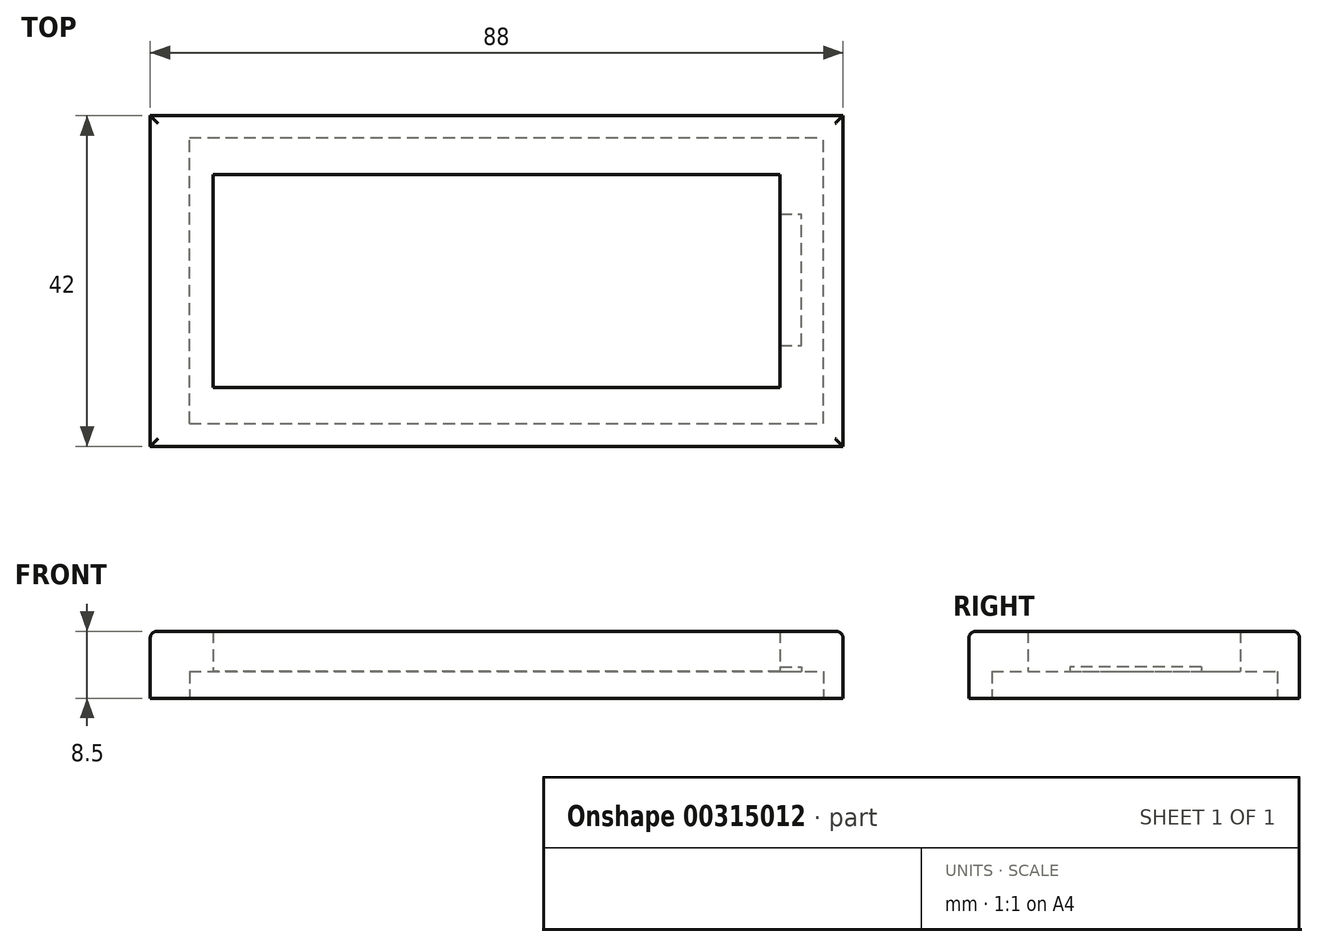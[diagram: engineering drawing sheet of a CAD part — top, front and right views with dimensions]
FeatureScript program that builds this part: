
annotation { "Feature Type Name" : "Feature", "Feature Type Description" : "" }
export const myFeature = defineFeature(function(context is Context, id is Id, definition is map)
    precondition{}
    {
        {
            var Q0;
            Q0=qCreatedBy(makeId("Top.planeOp"),FACE);
            var sketch = newSketch(context, id + "F0", { "sketchPlane" : qUnion([Q0])});
            skLineSegment(sketch, "E0", {"start": v(-44, 21) * mm, "end": v(44, 21) * mm});
            skLineSegment(sketch, "E1", {"start": v(44, 21) * mm, "end": v(44, -21) * mm});
            skLineSegment(sketch, "E2", {"start": v(44, -21) * mm, "end": v(-44, -21) * mm});
            skLineSegment(sketch, "E3", {"start": v(-44, -21) * mm, "end": v(-44, 21) * mm});
            skLineSegment(sketch, "E4.bottom", {"start": v(-36, 13.5) * mm, "end": v(36, 13.5) * mm});
            skLineSegment(sketch, "E4.top", {"start": v(-36, -13.5) * mm, "end": v(36, -13.5) * mm});
            skLineSegment(sketch, "E4.left", {"start": v(-36, 13.5) * mm, "end": v(-36, -13.5) * mm});
            skLineSegment(sketch, "E4.right", {"start": v(36, 13.5) * mm, "end": v(36, -13.5) * mm});
            skLineSegment(sketch, "E5", {"start": v(0, 21) * mm, "end": v(0, 13.5) * mm, "construction": true});
            skPoint(sketch, "E5.endSnap0", {"position": v(0, 13.5) * mm});
            skLineSegment(sketch, "E6", {"start": v(0, -13.5) * mm, "end": v(0, -21) * mm, "construction": true});
            skLineSegment(sketch, "E7", {"start": v(-44, 0) * mm, "end": v(-36, 0) * mm, "construction": true});
            skLineSegment(sketch, "E8", {"start": v(36, 0) * mm, "end": v(44, 0) * mm, "construction": true});
            skLineSegment(sketch, "E9", {"start": v(0, 0) * mm, "end": v(44, 0) * mm, "construction": true});
            skLineSegment(sketch, "E10", {"start": v(0, 0) * mm, "end": v(-44, 0) * mm, "construction": true});
            skLineSegment(sketch, "E11", {"start": v(0, 21) * mm, "end": v(0, -21) * mm, "construction": true});
            skSolve(sketch);
        }
        {
            var Q0;
            Q0=makeQuery(id+"F0.imprint","IMPRINT",FACE,{"disambiguationData":[TD([[makeQuery(id+"F0.imprint","IMPRINT",EDGE,{"derivedFrom":sQuery(id+"F0.wireOp",EDGE,"E0")}),-1.0]])]});
            extrude(context, id + "F1", {"entities" : qUnion([Q0]), "depth" : 8.5 * mm});
        }
        {
            var Q0;
            Q0=makeQuery(id+"F1.opExtrude","CAP_FACE",FACE,{"disambiguationData":[OSD([sQuery(id+"F0.wireOp",EDGE,"E0"),sQuery(id+"F0.wireOp",EDGE,"E1"),sQuery(id+"F0.wireOp",EDGE,"E2"),sQuery(id+"F0.wireOp",EDGE,"E3"),sQuery(id+"F0.wireOp",EDGE,"E4.bottom"),sQuery(id+"F0.wireOp",EDGE,"E4.top"),sQuery(id+"F0.wireOp",EDGE,"E4.left"),sQuery(id+"F0.wireOp",EDGE,"E4.right")])],"isStart":true});
            var sketch = newSketch(context, id + "F2", { "sketchPlane" : qUnion([Q0])});
            skLineSegment(sketch, "E12.bottom", {"start": v(36, 8.2) * mm, "end": v(38.75, 8.2) * mm});
            skLineSegment(sketch, "E12.top", {"start": v(36, -8.5) * mm, "end": v(38.75, -8.5) * mm});
            skLineSegment(sketch, "E12.left", {"start": v(36, 8.2) * mm, "end": v(36, -8.5) * mm});
            skLineSegment(sketch, "E12.right", {"start": v(38.75, 8.2) * mm, "end": v(38.75, -8.5) * mm});
            skLineSegment(sketch, "E13.left", {"start": v(38.75, 3.1) * mm, "end": v(38.75, -2.8) * mm});
            skLineSegment(sketch, "E14", {"start": v(38.75, 3.1) * mm, "end": v(41.5, 3.1) * mm});
            skLineSegment(sketch, "E15", {"start": v(41.5, 3.1) * mm, "end": v(41.5, -2.8) * mm});
            skLineSegment(sketch, "E16.bottom", {"start": v(-39, 18.1) * mm, "end": v(41.5, 18.1) * mm});
            skLineSegment(sketch, "E16.top", {"start": v(-39, -18.2) * mm, "end": v(41.5, -18.2) * mm});
            skLineSegment(sketch, "E16.left", {"start": v(-39, 18.1) * mm, "end": v(-39, -18.2) * mm});
            skLineSegment(sketch, "E16.right", {"start": v(41.5, 18.1) * mm, "end": v(41.5, -18.2) * mm});
            skLineSegment(sketch, "E17", {"start": v(38.75, -2.8) * mm, "end": v(41.5, -2.8) * mm});
            skSolve(sketch);
        }
        {
            var Q0;
            {var subQ1=sQuery(id+"F2.wireOp",EDGE,"E12.bottom");Q0=makeQuery(id+"F2.imprint","IMPRINT",FACE,{"disambiguationData":[TD([[makeQuery(id+"F2.imprint","IMPRINT",EDGE,{"derivedFrom":subQ1}),-1.0]])]});}
            extrude(context, id + "F3", {"entities" : qUnion([Q0]), "operationType" : NewBodyOperationType.REMOVE, "oppositeDirection" : true, "depth" : 4 * mm});
        }
        {
            var Q0;
            Q0=qSketchRegion(id+"F2",true);
            extrude(context, id + "F4", {"entities" : qUnion([Q0]), "operationType" : NewBodyOperationType.REMOVE, "oppositeDirection" : true, "depth" : 3.4 * mm});
        }
        {
            var Q0;
            Q0=makeQuery(id+"F1.opExtrude","CAP_EDGE",EDGE,{"disambiguationData":[OSD([sQuery(id+"F0.wireOp",EDGE,"E2")])],"isStart":false});
            var Q1;
            Q1=makeQuery(id+"F1.opExtrude","CAP_EDGE",EDGE,{"disambiguationData":[OSD([sQuery(id+"F0.wireOp",EDGE,"E1")])],"isStart":false});
            var Q2;
            Q2=makeQuery(id+"F1.opExtrude","CAP_EDGE",EDGE,{"disambiguationData":[OSD([sQuery(id+"F0.wireOp",EDGE,"E3")])],"isStart":false});
            var Q3;
            Q3=makeQuery(id+"F1.opExtrude","CAP_EDGE",EDGE,{"disambiguationData":[OSD([sQuery(id+"F0.wireOp",EDGE,"E0")])],"isStart":false});
            fillet(context, id + "F5", {"entities" : qUnion([Q0, Q1, Q2, Q3]), "radius" : 1 * mm, "tangentPropagation" : true, "rho" : 0.5, "crossSection" : FilletCrossSection.CONIC, "allowEdgeOverflow" : false});
        }
    });
